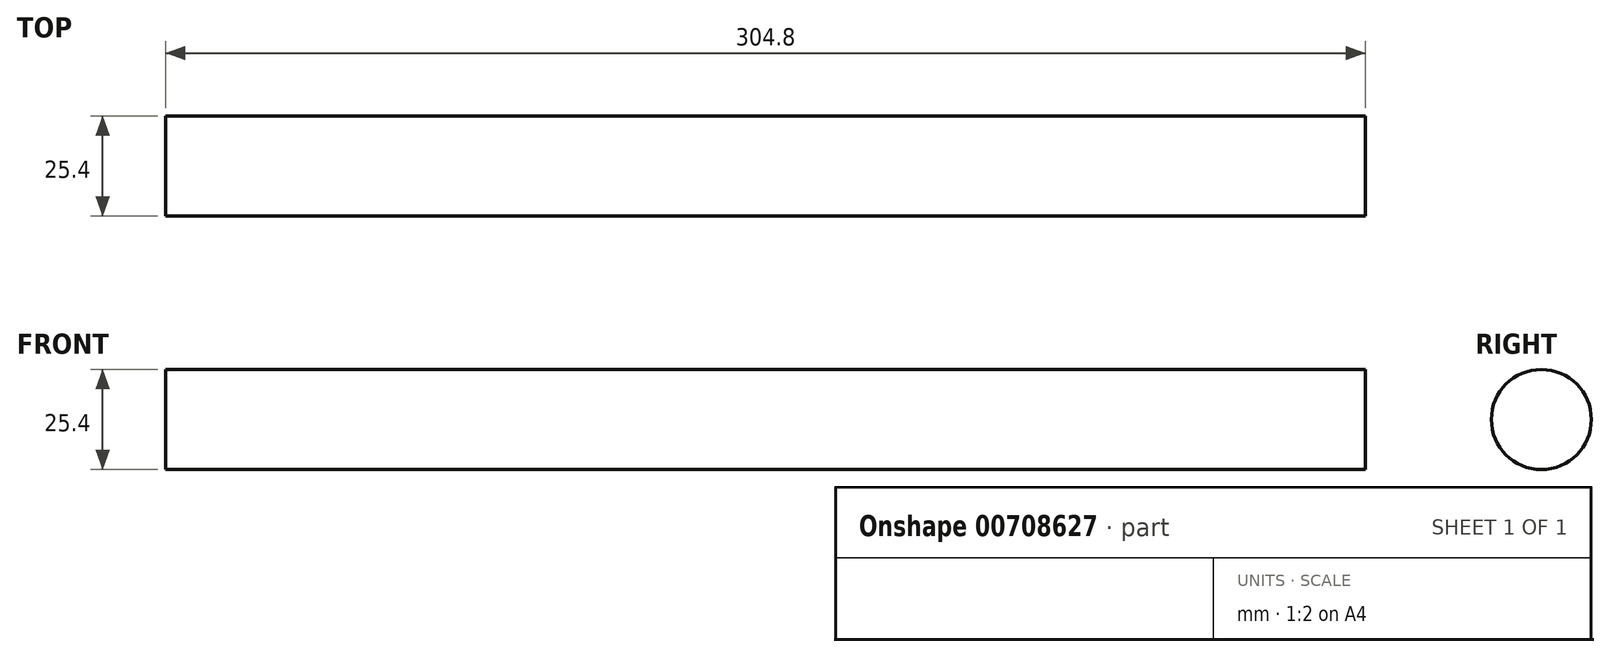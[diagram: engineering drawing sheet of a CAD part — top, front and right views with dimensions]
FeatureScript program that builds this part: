
annotation { "Feature Type Name" : "Feature", "Feature Type Description" : "" }
export const myFeature = defineFeature(function(context is Context, id is Id, definition is map)
    precondition{}
    {
        {
            var Q0;
            Q0=qCreatedBy(makeId("Right.planeOp"),FACE);
            var sketch = newSketch(context, id + "F0", { "sketchPlane" : qUnion([Q0])});
            skCircle(sketch, "E0", {"center": v(0, 0) * mm, "radius": 12.7 * mm});
            skSolve(sketch);
        }
        {
            var Q0;
            Q0 = qSketchRegion(id + "F0", true);
            var Q1;
            Q1=sQuery(id+"F0.wireOp",EDGE,"E0");
            extrude(context, id + "F1", {"entities" : qUnion([Q0]), "surfaceEntities" : qUnion([Q1]), "endBound" : BoundingType.SYMMETRIC, "depth" : 304.8 * mm, "offsetDistance" : 25 * mm});
        }
    });
